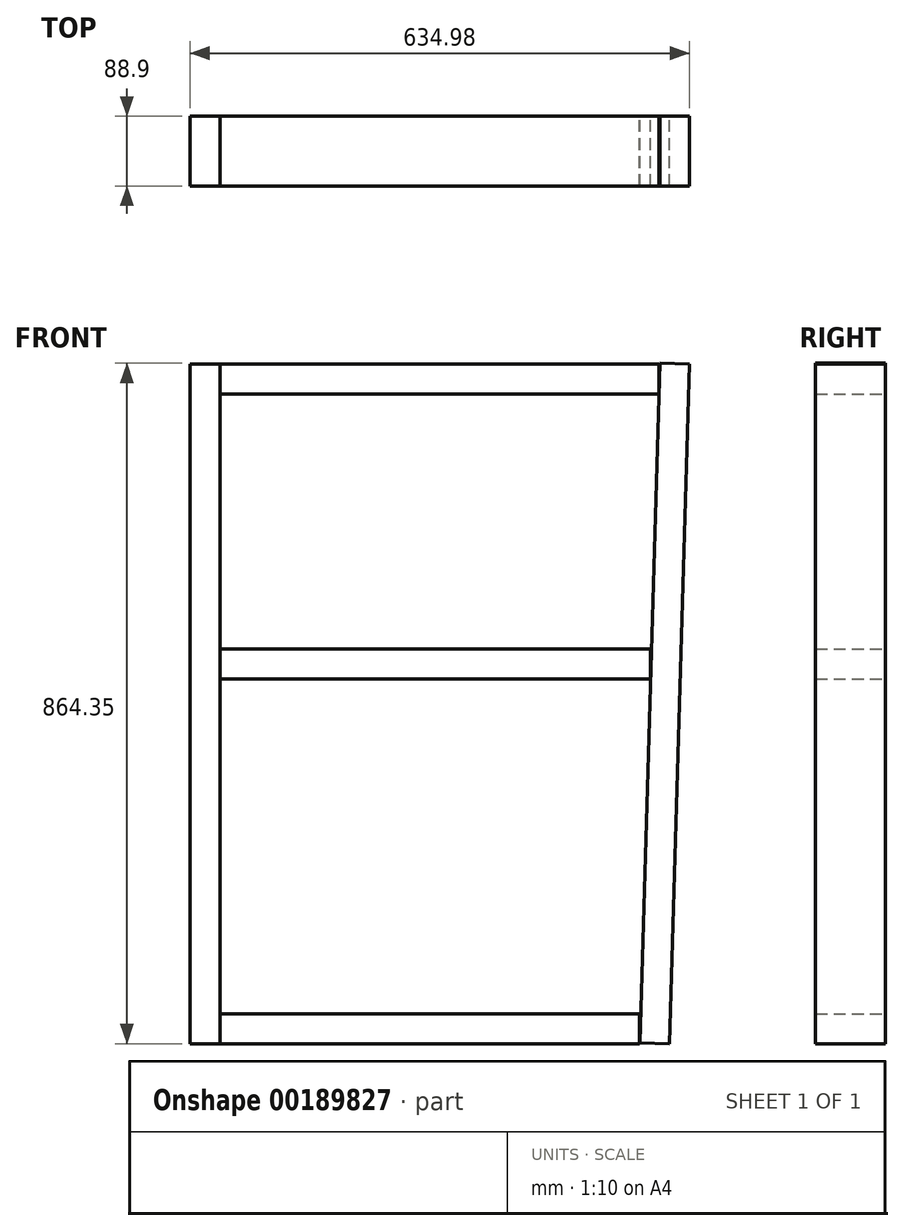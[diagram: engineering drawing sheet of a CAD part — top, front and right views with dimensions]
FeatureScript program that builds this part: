
annotation { "Feature Type Name" : "Feature", "Feature Type Description" : "" }
export const myFeature = defineFeature(function(context is Context, id is Id, definition is map)
    precondition{}
    {
        {
            var Q0;
            Q0=qCreatedBy(makeId("Front.planeOp"),FACE);
            var sketch = newSketch(context, id + "F0", { "sketchPlane" : qUnion([Q0])});
            skLineSegment(sketch, "E0.bottom", {"start": v(-571.5, 863.6) * mm, "end": v(-533.4, 863.6) * mm});
            skLineSegment(sketch, "E0.top", {"start": v(-571.5, 0) * mm, "end": v(-533.4, 0) * mm});
            skLineSegment(sketch, "E0.left", {"start": v(-571.5, 863.6) * mm, "end": v(-571.5, 0) * mm});
            skLineSegment(sketch, "E0.right", {"start": v(-533.4, 863.6) * mm, "end": v(-533.4, 0) * mm});
            skLineSegment(sketch, "E1", {"start": v(25.4, 864.35) * mm, "end": v(63.48, 863.23) * mm});
            skLineSegment(sketch, "E2", {"start": v(63.48, 863.23) * mm, "end": v(38.08, 0) * mm});
            skLineSegment(sketch, "E3", {"start": v(38.08, 0) * mm, "end": v(0, 1.12) * mm});
            skLineSegment(sketch, "E4", {"start": v(0, 1.12) * mm, "end": v(25.4, 864.35) * mm});
            skSolve(sketch);
        }
        {
            var Q0;
            Q0 = qSketchRegion(id + "F0", true);
            extrude(context, id + "F1", {"entities" : qUnion([Q0]), "depth" : 88.9 * mm});
        }
        {
            var Q0;
            Q0=qCreatedBy(makeId("Front.planeOp"),FACE);
            var sketch = newSketch(context, id + "F2", { "sketchPlane" : qUnion([Q0])});
            skLineSegment(sketch, "E5.bottom", {"start": v(-533.4, 863.6) * mm, "end": v(24.26, 863.6) * mm});
            skLineSegment(sketch, "E5.top", {"start": v(-533.4, 825.5) * mm, "end": v(24.26, 825.5) * mm});
            skLineSegment(sketch, "E5.left", {"start": v(-533.4, 863.6) * mm, "end": v(-533.4, 825.5) * mm});
            skLineSegment(sketch, "E5.right", {"start": v(24.26, 863.6) * mm, "end": v(24.26, 825.5) * mm});
            skLineSegment(sketch, "E6.bottom", {"start": v(-533.4, 0) * mm, "end": v(-0.03, 0) * mm});
            skLineSegment(sketch, "E6.top", {"start": v(-533.4, 38.1) * mm, "end": v(-0.03, 38.1) * mm});
            skLineSegment(sketch, "E6.left", {"start": v(-533.4, 0) * mm, "end": v(-533.4, 38.1) * mm});
            skLineSegment(sketch, "E6.right", {"start": v(-0.03, 0) * mm, "end": v(-0.03, 38.1) * mm});
            skLineSegment(sketch, "E7.bottom", {"start": v(-533.4, 501.65) * mm, "end": v(13.6, 501.65) * mm});
            skLineSegment(sketch, "E7.top", {"start": v(-533.4, 463.55) * mm, "end": v(13.6, 463.55) * mm});
            skLineSegment(sketch, "E7.left", {"start": v(-533.4, 501.65) * mm, "end": v(-533.4, 463.55) * mm});
            skLineSegment(sketch, "E7.right", {"start": v(13.6, 501.65) * mm, "end": v(13.6, 463.55) * mm});
            skSolve(sketch);
        }
        {
            var Q0;
            Q0 = qSketchRegion(id + "F2", true);
            extrude(context, id + "F3", {"entities" : qUnion([Q0]), "depth" : 88.9 * mm});
        }
    });
